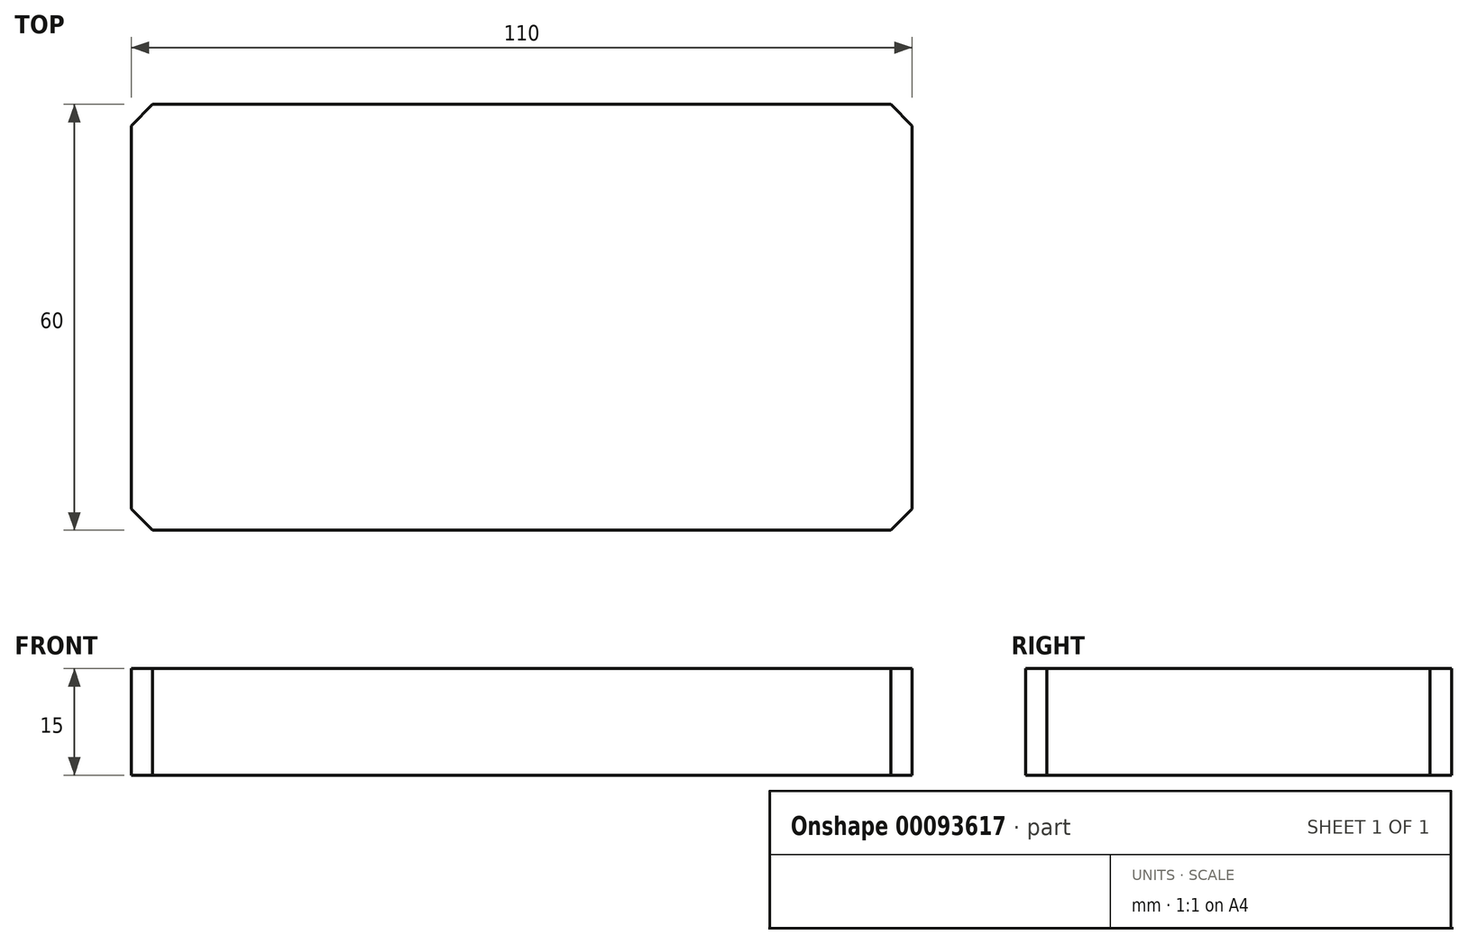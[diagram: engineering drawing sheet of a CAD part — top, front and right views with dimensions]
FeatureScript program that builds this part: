
annotation { "Feature Type Name" : "Feature", "Feature Type Description" : "" }
export const myFeature = defineFeature(function(context is Context, id is Id, definition is map)
    precondition{}
    {
        {
            var Q0;
            Q0=qCreatedBy(makeId("Top.planeOp"),FACE);
            var sketch = newSketch(context, id + "F0", { "sketchPlane" : qUnion([Q0])});
            skLineSegment(sketch, "E0", {"start": v(-53.27, 23.86) * mm, "end": v(56.73, 23.86) * mm});
            skLineSegment(sketch, "E1", {"start": v(-53.27, 23.86) * mm, "end": v(-53.27, -36.14) * mm});
            skLineSegment(sketch, "E2", {"start": v(-53.27, -36.14) * mm, "end": v(56.73, -36.14) * mm});
            skLineSegment(sketch, "E3", {"start": v(56.73, -36.14) * mm, "end": v(56.73, 23.86) * mm});
            skSolve(sketch);
        }
        {
            var Q0;
            Q0=makeQuery(id+"F0.imprint","IMPRINT",FACE,{"disambiguationData":[TD([[makeQuery(id+"F0.imprint","IMPRINT",EDGE,{"derivedFrom":sQuery(id+"F0.wireOp",EDGE,"E0")}),-1.0]])]});
            extrude(context, id + "F1", {"entities" : qUnion([Q0]), "depth" : 15 * mm});
        }
        {
            var Q0;
            Q0=makeQuery(id+"F1.opExtrude","SWEPT_EDGE",EDGE,{"disambiguationData":[OSD([sQuery(id+"F0.wireOp",EDGE,"E1"),sQuery(id+"F0.wireOp",EDGE,"E2")])]});
            var Q1;
            Q1=makeQuery(id+"F1.opExtrude","SWEPT_EDGE",EDGE,{"disambiguationData":[OSD([sQuery(id+"F0.wireOp",EDGE,"E2"),sQuery(id+"F0.wireOp",EDGE,"E3")])]});
            var Q2;
            Q2=makeQuery(id+"F1.opExtrude","SWEPT_EDGE",EDGE,{"disambiguationData":[OSD([sQuery(id+"F0.wireOp",EDGE,"E0"),sQuery(id+"F0.wireOp",EDGE,"E3")])]});
            var Q3;
            Q3=makeQuery(id+"F1.opExtrude","SWEPT_EDGE",EDGE,{"disambiguationData":[OSD([sQuery(id+"F0.wireOp",EDGE,"E0"),sQuery(id+"F0.wireOp",EDGE,"E1")])]});
            chamfer(context, id + "F2", {"entities" : qUnion([Q0, Q1, Q2, Q3]), "width" : 3 * mm, "tangentPropagation" : true});
        }
    });
